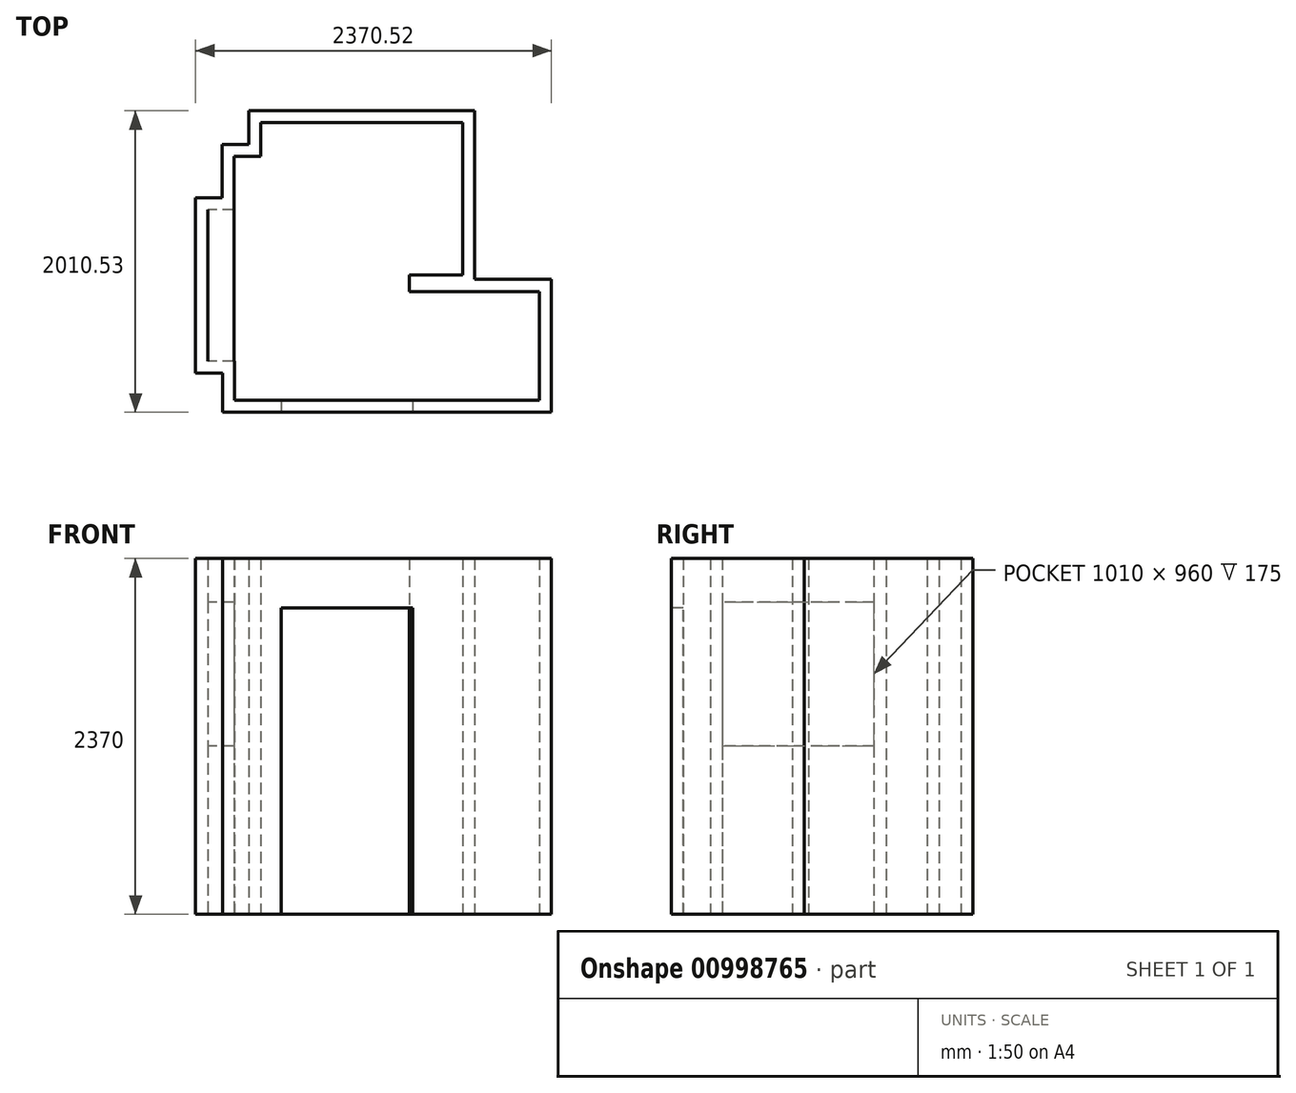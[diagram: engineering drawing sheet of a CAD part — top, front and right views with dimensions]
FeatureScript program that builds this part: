
annotation { "Feature Type Name" : "Feature", "Feature Type Description" : "" }
export const myFeature = defineFeature(function(context is Context, id is Id, definition is map)
    precondition{}
    {
        {
            var Q0;
            Q0=qCreatedBy(makeId("Top.planeOp"),FACE);
            var sketch = newSketch(context, id + "F0", { "sketchPlane" : qUnion([Q0])});
            skLineSegment(sketch, "E0", {"start": v(1100.75, -767.07) * mm, "end": v(1100.75, -42.07) * mm});
            skLineSegment(sketch, "E1", {"start": v(1100.75, -42.07) * mm, "end": v(235.75, -42.07) * mm});
            skLineSegment(sketch, "E2", {"start": v(235.75, -42.07) * mm, "end": v(235.75, 67.93) * mm});
            skLineSegment(sketch, "E3", {"start": v(235.75, 67.93) * mm, "end": v(590.75, 67.93) * mm});
            skLineSegment(sketch, "E4", {"start": v(590.75, 67.93) * mm, "end": v(590.75, 1082.93) * mm});
            skLineSegment(sketch, "E5", {"start": v(590.75, 1082.93) * mm, "end": v(-754.25, 1082.93) * mm});
            skLineSegment(sketch, "E6", {"start": v(-754.25, 1082.93) * mm, "end": v(-754.25, 857.93) * mm});
            skLineSegment(sketch, "E7", {"start": v(-754.25, 857.93) * mm, "end": v(-934.25, 857.93) * mm});
            skLineSegment(sketch, "E8", {"start": v(-934.25, 857.93) * mm, "end": v(-934.25, 502.93) * mm});
            skLineSegment(sketch, "E9", {"start": v(-934.25, 502.93) * mm, "end": v(-1109.25, 502.93) * mm});
            skLineSegment(sketch, "E10", {"start": v(-1109.25, -507.07) * mm, "end": v(-929.25, -507.07) * mm});
            skLineSegment(sketch, "E11", {"start": v(-929.25, -507.07) * mm, "end": v(-929.25, -767.07) * mm});
            skLineSegment(sketch, "E12", {"start": v(-1109.25, 502.93) * mm, "end": v(-1109.25, -507.07) * mm});
            skLineSegment(sketch, "E13", {"start": v(-929.25, -767.07) * mm, "end": v(1100.75, -767.07) * mm});
            skLineSegment(sketch, "E14.0", {"start": v(-1014.5, 583.19) * mm, "end": v(-1189.5, 583.19) * mm});
            skLineSegment(sketch, "E14.1", {"start": v(1181.01, -847.34) * mm, "end": v(1181.01, 38.19) * mm});
            skLineSegment(sketch, "E14.2", {"start": v(-1009.5, -847.34) * mm, "end": v(1181.01, -847.34) * mm});
            skLineSegment(sketch, "E14.3", {"start": v(-1009.5, -587.34) * mm, "end": v(-1009.5, -847.34) * mm});
            skLineSegment(sketch, "E14.4", {"start": v(-1189.5, -587.34) * mm, "end": v(-1009.5, -587.34) * mm});
            skLineSegment(sketch, "E14.5", {"start": v(1181.01, 38.19) * mm, "end": v(671.01, 38.19) * mm});
            skLineSegment(sketch, "E14.6", {"start": v(-1189.5, 583.19) * mm, "end": v(-1189.5, -587.34) * mm});
            skLineSegment(sketch, "E14.7", {"start": v(671.01, 38.19) * mm, "end": v(671.01, 1163.19) * mm});
            skLineSegment(sketch, "E14.8", {"start": v(671.01, 1163.19) * mm, "end": v(-834.5, 1163.19) * mm});
            skLineSegment(sketch, "E14.9", {"start": v(-834.5, 1163.19) * mm, "end": v(-834.5, 938.19) * mm});
            skLineSegment(sketch, "E14.10", {"start": v(-834.5, 938.19) * mm, "end": v(-1014.5, 938.19) * mm});
            skLineSegment(sketch, "E14.11", {"start": v(-1014.5, 938.19) * mm, "end": v(-1014.5, 583.19) * mm});
            skSolve(sketch);
        }
        {
            var Q0;
            Q0=makeQuery(id+"F0.imprint","IMPRINT",FACE,{"disambiguationData":[TD([[makeQuery(id+"F0.imprint","IMPRINT",EDGE,{"derivedFrom":sQuery(id+"F0.wireOp",EDGE,"E0")}),-1.0]])]});
            extrude(context, id + "F1", {"entities" : qUnion([Q0]), "depth" : 2370 * mm, "offsetDistance" : 25.4 * mm});
        }
        {
            var Q0;
            Q0=makeQuery(id+"F1.opExtrude","SWEPT_FACE",FACE,{"disambiguationData":[OSD([sQuery(id+"F0.wireOp",EDGE,"E14.2")])]});
            var sketch = newSketch(context, id + "F2", { "sketchPlane" : qUnion([Q0])});
            skLineSegment(sketch, "E15", {"start": v(-1009.5, 0) * mm, "end": v(-619.5, 0) * mm});
            skLineSegment(sketch, "E16", {"start": v(-619.5, 0) * mm, "end": v(255.5, 0) * mm});
            skLineSegment(sketch, "E17", {"start": v(-619.5, 0) * mm, "end": v(-619.5, 2040) * mm});
            skLineSegment(sketch, "E18", {"start": v(-619.5, 2040) * mm, "end": v(255.5, 2040) * mm});
            skLineSegment(sketch, "E19", {"start": v(255.5, 2040) * mm, "end": v(255.5, 0) * mm});
            skSolve(sketch);
        }
        {
            var Q0;
            Q0 = qSketchRegion(id + "F2", true);
            extrude(context, id + "F3", {"entities" : qUnion([Q0]), "operationType" : NewBodyOperationType.REMOVE, "endBound" : BoundingType.UP_TO_NEXT, "oppositeDirection" : true, "depth" : 25.4 * mm, "offsetDistance" : 25.4 * mm});
        }
        {
            var Q0;
            Q0=makeQuery(id+"F1.opExtrude","SWEPT_FACE",FACE,{"disambiguationData":[OSD([sQuery(id+"F0.wireOp",EDGE,"E12")])]});
            var sketch = newSketch(context, id + "F4", { "sketchPlane" : qUnion([Q0])});
            skLineSegment(sketch, "E20", {"start": v(502.93, 2080) * mm, "end": v(0, 2080) * mm});
            skLineSegment(sketch, "E21", {"start": v(502.93, 1120) * mm, "end": v(-139.11, 1120) * mm});
            skLineSegment(sketch, "E22", {"start": v(0, 2080) * mm, "end": v(-507.07, 2080) * mm});
            skLineSegment(sketch, "E23", {"start": v(-507.07, 2080) * mm, "end": v(-507.07, 2370) * mm});
            skLineSegment(sketch, "E24", {"start": v(-507.07, 2370) * mm, "end": v(502.93, 2370) * mm});
            skLineSegment(sketch, "E25", {"start": v(502.93, 2370) * mm, "end": v(502.93, 2080) * mm});
            skLineSegment(sketch, "E26", {"start": v(-139.11, 1120) * mm, "end": v(-507.07, 1120) * mm});
            skLineSegment(sketch, "E27", {"start": v(-507.07, 1120) * mm, "end": v(-507.07, 0) * mm});
            skLineSegment(sketch, "E28", {"start": v(-507.07, 0) * mm, "end": v(502.93, 0) * mm});
            skLineSegment(sketch, "E29", {"start": v(502.93, 0) * mm, "end": v(502.93, 1120) * mm});
            skSolve(sketch);
        }
        {
            var Q0;
            Q0=makeQuery(id+"F4.imprint","IMPRINT",FACE,{"disambiguationData":[TD([[makeQuery(id+"F4.imprint","IMPRINT",EDGE,{"derivedFrom":sQuery(id+"F4.wireOp",EDGE,"E20")}),-1.0]])]});
            var Q1;
            Q1=makeQuery(id+"F1.opExtrude","CAP_VERTEX",VERTEX,{"disambiguationData":[OSD([sQuery(id+"F0.wireOp",EDGE,"E8"),sQuery(id+"F0.wireOp",EDGE,"E9")])],"isStart":false});
            extrude(context, id + "F5", {"entities" : qUnion([Q0]), "operationType" : NewBodyOperationType.ADD, "endBound" : BoundingType.UP_TO_VERTEX, "depth" : 149.86 * mm, "endBoundEntityVertex" : qUnion([Q1]), "offsetDistance" : 25.4 * mm});
        }
        {
            var Q0;
            Q0=makeQuery(id+"F4.imprint","IMPRINT",FACE,{"disambiguationData":[TD([[makeQuery(id+"F4.imprint","IMPRINT",EDGE,{"derivedFrom":sQuery(id+"F4.wireOp",EDGE,"E21")}),1.0]])]});
            var Q1;
            Q1=makeQuery(id+"F1.opExtrude","CAP_VERTEX",VERTEX,{"disambiguationData":[OSD([sQuery(id+"F0.wireOp",EDGE,"E8"),sQuery(id+"F0.wireOp",EDGE,"E9")])],"isStart":true});
            extrude(context, id + "F6", {"entities" : qUnion([Q0]), "operationType" : NewBodyOperationType.ADD, "endBound" : BoundingType.UP_TO_VERTEX, "depth" : 25.4 * mm, "endBoundEntityVertex" : qUnion([Q1]), "offsetDistance" : 25.4 * mm});
        }
        {
            var Q0;
            Q0 = qSketchRegion(id + "F4", true);
            extrude(context, id + "F7", {"entities" : qUnion([Q0]), "depth" : 0.1 * mm, "offsetDistance" : 25.4 * mm});
        }
        {
            var Q0;
            {var subQ3=sQuery(id+"F4.wireOp",EDGE,"E20");Q0=makeQuery(id+"F4.imprint","IMPRINT",FACE,{"disambiguationData":[TD([[makeQuery(id+"F4.imprint","IMPRINT",EDGE,{"derivedFrom":subQ3}),1.0]])]});}
            extrude(context, id + "F8", {"entities" : qUnion([Q0]), "depth" : 1 * mm, "offsetDistance" : 25.4 * mm});
        }
    });
